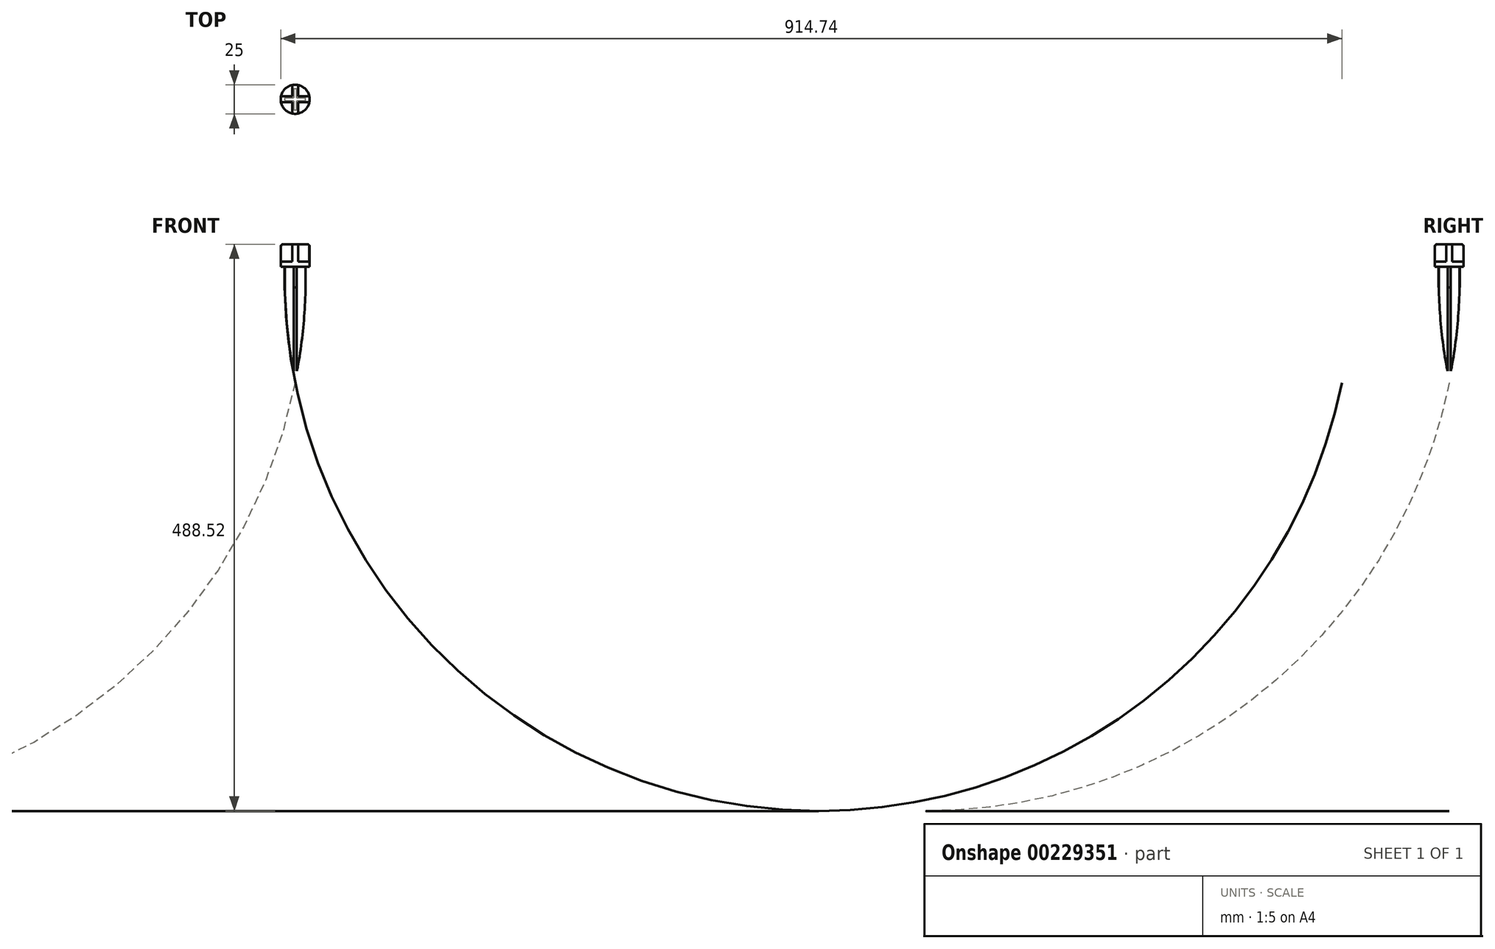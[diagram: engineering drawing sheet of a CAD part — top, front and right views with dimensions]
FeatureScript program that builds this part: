
annotation { "Feature Type Name" : "Feature", "Feature Type Description" : "" }
export const myFeature = defineFeature(function(context is Context, id is Id, definition is map)
    precondition{}
    {
        {
            var Q0;
            Q0=qCreatedBy(makeId("Top.planeOp"),FACE);
            var sketch = newSketch(context, id + "F0", { "sketchPlane" : qUnion([Q0])});
            skCircle(sketch, "E0", {"center": v(0, 0) * mm, "radius": 12.5 * mm});
            skSolve(sketch);
        }
        {
            var Q0;
            Q0=qSketchRegion(id+"F0",true);
            extrude(context, id + "F1", {"entities" : qUnion([Q0]), "depth" : 17.5 * mm});
        }
        {
            var Q0;
            Q0=makeQuery(id+"F1.opExtrude","CAP_EDGE",EDGE,{"disambiguationData":[OSD([sQuery(id+"F0.wireOp",EDGE,"E0")])],"isStart":false});
            fillet(context, id + "F2", {"entities" : qUnion([Q0]), "radius" : 2 * mm, "tangentPropagation" : true, "allowEdgeOverflow" : false});
        }
        {
            var Q0;
            Q0=makeQuery(id+"F1.opExtrude","CAP_FACE",FACE,{"disambiguationData":[OSD([sQuery(id+"F0.wireOp",EDGE,"E0")])],"isStart":true});
            var sketch = newSketch(context, id + "F3", { "sketchPlane" : qUnion([Q0])});
            skCircle(sketch, "E1", {"center": v(0, 0) * mm, "radius": 12.5 * mm});
            skSolve(sketch);
        }
        {
            var Q0;
            Q0=qSketchRegion(id+"F3",true);
            extrude(context, id + "F4", {"entities" : qUnion([Q0]), "operationType" : NewBodyOperationType.ADD, "depth" : 2 * mm});
        }
        {
            var Q0;
            Q0=makeQuery(id+"F4.opExtrude","CAP_FACE",FACE,{"disambiguationData":[OSD([sQuery(id+"F3.wireOp",EDGE,"E1")])],"isStart":false});
            var sketch = newSketch(context, id + "F5", { "sketchPlane" : qUnion([Q0])});
            skCircle(sketch, "E2", {"center": v(0, 0) * mm, "radius": 9.05 * mm});
            skSolve(sketch);
        }
        {
            var Q0;
            Q0=qSketchRegion(id+"F5",true);
            extrude(context, id + "F6", {"entities" : qUnion([Q0]), "operationType" : NewBodyOperationType.ADD, "depth" : 100 * mm});
        }
        {
            var Q0;
            Q0=qCreatedBy(makeId("Front.planeOp"),FACE);
            var sketch = newSketch(context, id + "F7", { "sketchPlane" : qUnion([Q0])});
            skLineSegment(sketch, "E3", {"start": v(0, -2) * mm, "end": v(0, 0) * mm});
            skLineSegment(sketch, "E4", {"start": v(0, -2) * mm, "end": v(0, -102) * mm});
            skArc(sketch, "E5", {"start": v(-9.05, -2) * mm, "mid": v(-7.26, -52.25) * mm, "end": v(0, -102) * mm});
            skLineSegment(sketch, "E6", {"start": v(0, -102) * mm, "end": v(-9.05, -102) * mm});
            skLineSegment(sketch, "E7", {"start": v(-9.05, -102) * mm, "end": v(-9.05, -2) * mm});
            skArc(sketch, "E8.MirrorCS", {"start": v(9.05, -2) * mm, "mid": v(7.26, -52.25) * mm, "end": v(0, -102) * mm});
            skLineSegment(sketch, "E9.MirrorCS", {"start": v(9.05, -102) * mm, "end": v(9.05, -2) * mm});
            skLineSegment(sketch, "E10.MirrorCS", {"start": v(0, -102) * mm, "end": v(9.05, -102) * mm});
            skSolve(sketch);
        }
        {
            var Q0;
            Q0=qSketchRegion(id+"F7",true);
            var Q1;
            Q1=sQuery(id+"F7.wireOp",EDGE,"E4");
            revolve(context, id + "F8", {"operationType" : NewBodyOperationType.REMOVE, "entities" : qUnion([Q0]), "axis" : qUnion([Q1]), "revolveType" : RevolveType.ONE_DIRECTION, "angle" : 180 * degree});
        }
        {
            var Q0;
            Q0=makeQuery(id+"F4.opExtrude","CAP_FACE",FACE,{"disambiguationData":[OSD([sQuery(id+"F3.wireOp",EDGE,"E1")])],"isStart":false});
            var sketch = newSketch(context, id + "F9", { "sketchPlane" : qUnion([Q0])});
            skLineSegment(sketch, "E11.0.0", {"start": v(-1.4, -7.42) * mm, "end": v(-1.4, -1.4) * mm});
            skLineSegment(sketch, "E11.0.1", {"start": v(-1.4, -1.4) * mm, "end": v(-7.42, -1.4) * mm});
            skLineSegment(sketch, "E11.0.3", {"start": v(-7.42, 1.4) * mm, "end": v(-1.4, 1.4) * mm});
            skLineSegment(sketch, "E11.0.4", {"start": v(-1.4, 1.4) * mm, "end": v(-1.4, 7.42) * mm});
            skLineSegment(sketch, "E11.0.6", {"start": v(1.4, 7.42) * mm, "end": v(1.4, 1.4) * mm});
            skLineSegment(sketch, "E11.0.7", {"start": v(1.4, 1.4) * mm, "end": v(7.42, 1.4) * mm});
            skLineSegment(sketch, "E11.0.9", {"start": v(7.42, -1.4) * mm, "end": v(1.4, -1.4) * mm});
            skLineSegment(sketch, "E11.0.10", {"start": v(1.4, -1.4) * mm, "end": v(1.4, -7.42) * mm});
            skLineSegment(sketch, "E12", {"start": v(7.42, 1.4) * mm, "end": v(12.42, 1.4) * mm});
            skLineSegment(sketch, "E13", {"start": v(7.42, -1.4) * mm, "end": v(12.42, -1.4) * mm});
            skLineSegment(sketch, "E14.MirrorCS", {"start": v(1.4, 7.42) * mm, "end": v(1.4, 12.42) * mm});
            skLineSegment(sketch, "E15.MirrorCS", {"start": v(-1.4, 7.42) * mm, "end": v(-1.4, 12.42) * mm});
            skLineSegment(sketch, "E16.MirrorCS", {"start": v(-7.42, 1.4) * mm, "end": v(-12.42, 1.4) * mm});
            skLineSegment(sketch, "E17.MirrorCS", {"start": v(-7.42, -1.4) * mm, "end": v(-12.42, -1.4) * mm});
            skLineSegment(sketch, "E18.MirrorCS", {"start": v(1.4, -7.42) * mm, "end": v(1.4, -12.42) * mm});
            skLineSegment(sketch, "E19.MirrorCS", {"start": v(-1.4, -7.42) * mm, "end": v(-1.4, -12.42) * mm});
            skLineSegment(sketch, "E20", {"start": v(1.4, -12.42) * mm, "end": v(12.42, -1.4) * mm});
            skLineSegment(sketch, "E21", {"start": v(-1.4, -12.42) * mm, "end": v(-12.42, -1.4) * mm});
            skLineSegment(sketch, "E22", {"start": v(12.42, 1.4) * mm, "end": v(1.4, 12.42) * mm});
            skLineSegment(sketch, "E23", {"start": v(-1.4, 12.42) * mm, "end": v(-12.42, 1.4) * mm});
            skSolve(sketch);
        }
        {
            var Q0;
            Q0=qSketchRegion(id+"F9",true);
            extrude(context, id + "F10", {"entities" : qUnion([Q0]), "operationType" : NewBodyOperationType.REMOVE, "endBound" : BoundingType.THROUGH_ALL, "depth" : 25 * mm});
        }
        {
            var Q0;
            Q0=makeQuery(id+"F1.opExtrude","CAP_FACE",FACE,{"disambiguationData":[OSD([sQuery(id+"F0.wireOp",EDGE,"E0")])],"isStart":false});
            var sketch = newSketch(context, id + "F11", { "sketchPlane" : qUnion([Q0])});
            skLineSegment(sketch, "E24", {"start": v(0, 12.1) * mm, "end": v(0, -17.1) * mm, "construction": true});
            skLineSegment(sketch, "E25.left", {"start": v(-2.5, 10.63) * mm, "end": v(-2.5, 2.5) * mm});
            skLineSegment(sketch, "E25.right", {"start": v(2.5, 10.63) * mm, "end": v(2.5, 2.5) * mm});
            skLineSegment(sketch, "E26", {"start": v(-12.07, 0) * mm, "end": v(12.7, 0) * mm, "construction": true});
            skPoint(sketch, "E27.oppositeSnap0", {"position": v(0, -2.5) * mm});
            skLineSegment(sketch, "E27.bottom", {"start": v(-10.63, 2.5) * mm, "end": v(-2.5, 2.5) * mm});
            skLineSegment(sketch, "E27.top", {"start": v(-12.07, -2.5) * mm, "end": v(-2.5, -2.5) * mm});
            skLineSegment(sketch, "E28.trimOffspring", {"start": v(2.5, 2.5) * mm, "end": v(10.63, 2.5) * mm});
            skLineSegment(sketch, "E29.trimOffspring", {"start": v(-2.5, -2.5) * mm, "end": v(-2.5, -10.63) * mm});
            skLineSegment(sketch, "E30.trimOffspring", {"start": v(2.5, -2.5) * mm, "end": v(10.63, -2.5) * mm});
            skLineSegment(sketch, "E31.trimOffspring", {"start": v(2.5, -2.5) * mm, "end": v(2.5, -10.63) * mm});
            skPoint(sketch, "E32.orphan", {"position": v(-2.5, 12.1) * mm});
            skPoint(sketch, "E33.orphan", {"position": v(-12.07, 2.5) * mm});
            skPoint(sketch, "E34.orphan", {"position": v(12.1, -2.5) * mm});
            skPoint(sketch, "E35.orphan", {"position": v(2.5, 12.1) * mm});
            skArc(sketch, "E36", {"start": v(-2.5, 13.37) * mm, "mid": v(-9.62, 9.62) * mm, "end": v(-13.37, 2.5) * mm});
            skLineSegment(sketch, "E37", {"start": v(-2.5, 10.63) * mm, "end": v(-2.5, 13.37) * mm});
            skLineSegment(sketch, "E38", {"start": v(2.5, 10.63) * mm, "end": v(2.5, 13.37) * mm});
            skLineSegment(sketch, "E39", {"start": v(10.63, 2.5) * mm, "end": v(13.37, 2.5) * mm});
            skLineSegment(sketch, "E40", {"start": v(10.63, -2.5) * mm, "end": v(13.37, -2.5) * mm});
            skLineSegment(sketch, "E41", {"start": v(2.5, -10.63) * mm, "end": v(2.5, -13.37) * mm});
            skLineSegment(sketch, "E42", {"start": v(-2.5, -10.63) * mm, "end": v(-2.5, -13.37) * mm});
            skLineSegment(sketch, "E43", {"start": v(-12.07, -2.5) * mm, "end": v(-13.37, -2.5) * mm});
            skLineSegment(sketch, "E44", {"start": v(-10.63, 2.5) * mm, "end": v(-13.37, 2.5) * mm});
            skArc(sketch, "E45.trimOffspring", {"start": v(-13.37, -2.5) * mm, "mid": v(-9.62, -9.62) * mm, "end": v(-2.5, -13.37) * mm});
            skArc(sketch, "E46.trimOffspring", {"start": v(2.5, -13.37) * mm, "mid": v(13.6, 0) * mm, "end": v(2.5, 13.37) * mm});
            skSolve(sketch);
        }
        {
            var Q0;
            {var subQ0=sQuery(id+"F11.wireOp",EDGE,"E29.trimOffspring");var subQ1=sQuery(id+"F11.wireOp",EDGE,"E27.top");var subQ2=makeQuery(id+"F11.imprint","INTERSECT",VERTEX,{"derivedFrom":[subQ1,subQ0]});Q0=makeQuery(id+"F11.imprint","IMPRINT",FACE,{"disambiguationData":[TD([[makeQuery(id+"F11.imprint","IMPRINT",EDGE,{"disambiguationData":[TD([[subQ2,1.0]])],"derivedFrom":subQ1}),-1.0]])]});}
            var Q1;
            {var subQ1=sQuery(id+"F11.wireOp",EDGE,"E42");Q1=makeQuery(id+"F11.imprint","IMPRINT",FACE,{"disambiguationData":[TD([[makeQuery(id+"F11.imprint","IMPRINT",EDGE,{"derivedFrom":subQ1}),-1.0]])]});}
            var Q2;
            {var subQ0=sQuery(id+"F11.wireOp",EDGE,"E28.trimOffspring");var subQ1=sQuery(id+"F11.wireOp",EDGE,"E25.right");var subQ2=makeQuery(id+"F11.imprint","INTERSECT",VERTEX,{"derivedFrom":[subQ1,subQ0]});Q2=makeQuery(id+"F11.imprint","IMPRINT",FACE,{"disambiguationData":[TD([[makeQuery(id+"F11.imprint","IMPRINT",EDGE,{"disambiguationData":[TD([[subQ2,1.0]])],"derivedFrom":subQ1}),1.0]])]});}
            var Q3;
            {var subQ1=sQuery(id+"F11.wireOp",EDGE,"E38");Q3=makeQuery(id+"F11.imprint","IMPRINT",FACE,{"disambiguationData":[TD([[makeQuery(id+"F11.imprint","IMPRINT",EDGE,{"derivedFrom":subQ1}),-1.0]])]});}
            var Q4;
            {var subQ0=sQuery(id+"F11.wireOp",EDGE,"E31.trimOffspring");var subQ1=sQuery(id+"F11.wireOp",EDGE,"E30.trimOffspring");var subQ2=makeQuery(id+"F11.imprint","INTERSECT",VERTEX,{"derivedFrom":[subQ1,subQ0]});Q4=makeQuery(id+"F11.imprint","IMPRINT",FACE,{"disambiguationData":[TD([[makeQuery(id+"F11.imprint","IMPRINT",EDGE,{"disambiguationData":[TD([[subQ2,-1.0]])],"derivedFrom":subQ1}),-1.0]])]});}
            var Q5;
            {var subQ1=sQuery(id+"F11.wireOp",EDGE,"E40");Q5=makeQuery(id+"F11.imprint","IMPRINT",FACE,{"disambiguationData":[TD([[makeQuery(id+"F11.imprint","IMPRINT",EDGE,{"derivedFrom":subQ1}),-1.0]])]});}
            var Q6;
            Q6=makeQuery(id+"F11.imprint","IMPRINT",FACE,{"disambiguationData":[TD([[makeQuery(id+"F11.imprint","IMPRINT",EDGE,{"derivedFrom":sQuery(id+"F11.wireOp",EDGE,"E36")}),1.0]])]});
            var Q7;
            {var subQ0=sQuery(id+"F11.wireOp",EDGE,"E27.bottom");var subQ1=sQuery(id+"F11.wireOp",EDGE,"E25.left");var subQ2=makeQuery(id+"F11.imprint","INTERSECT",VERTEX,{"derivedFrom":[subQ1,subQ0]});Q7=makeQuery(id+"F11.imprint","IMPRINT",FACE,{"disambiguationData":[TD([[makeQuery(id+"F11.imprint","IMPRINT",EDGE,{"disambiguationData":[TD([[subQ2,1.0]])],"derivedFrom":subQ1}),-1.0]])]});}
            var Q8;
            {var subQ7=sQuery(id+"F11.wireOp",EDGE,"E43");Q8=makeQuery(id+"F11.imprint","IMPRINT",FACE,{"disambiguationData":[TD([[makeQuery(id+"F11.imprint","IMPRINT",EDGE,{"derivedFrom":subQ7}),1.0]])]});}
            extrude(context, id + "F12", {"entities" : qUnion([Q0, Q1, Q2, Q3, Q4, Q5, Q6, Q7, Q8]), "operationType" : NewBodyOperationType.REMOVE, "oppositeDirection" : true, "depth" : 15 * mm});
        }
    });
